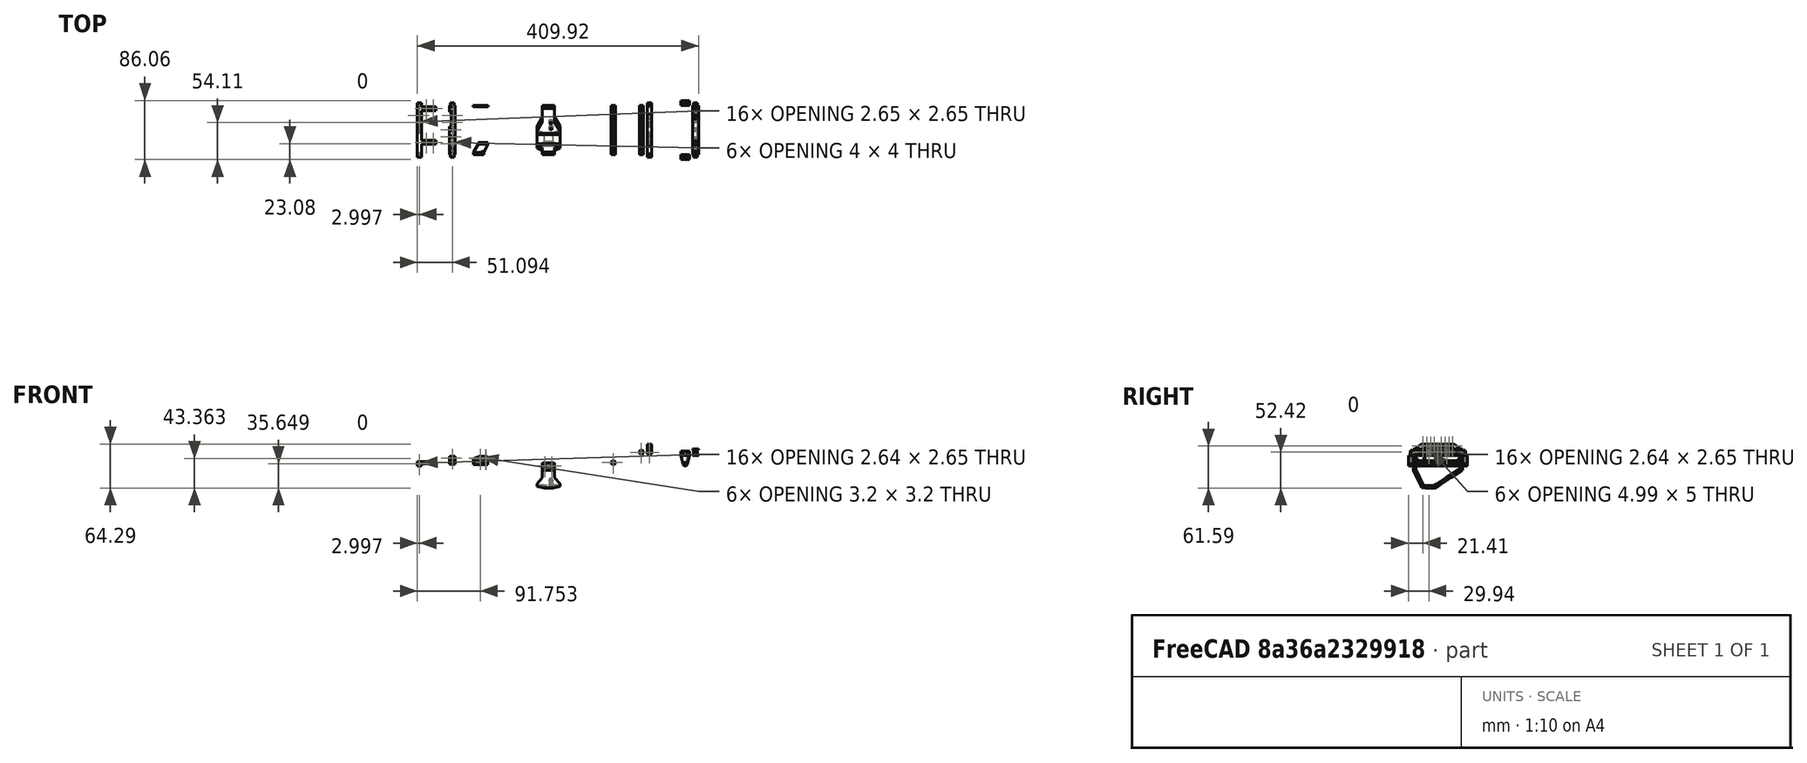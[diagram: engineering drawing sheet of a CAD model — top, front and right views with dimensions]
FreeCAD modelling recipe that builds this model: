
FCSTD DOCUMENT  (FreeCAD 1.0R39109 (Git))
Label: TF2
License: All rights reserved
LicenseURL: https://en.wikipedia.org/wiki/All_rights_reserved
objects: Part::Feature×4, Part::Refine×2, Mesh::Feature×1
note: 6 computed .brp shape members not serialized (recipe doc carries the construction recipe); baked Part::Feature solids carry a one-line shape summary decoded from their .brp

FEATURE [Mesh::Feature] Trail_Finder_2_Chassis
FEATURE [Part::Feature] Trail_Finder_2_Chassis001
  shape: bbox 445.6 x 96 x 74.94 mm, 36120 faces, 0 solids (baked)
FEATURE [Part::Feature] Trail_Finder_2_Chassis001_solid  label="Trail_Finder_2_Chassis001 (Solid)"
  shape: bbox 445.6 x 96 x 74.94 mm, 36104 faces (baked)
FEATURE [Part::Refine] Trail_Finder_2_Chassis001_solid001  label="Trail_Finder_2_Chassis001 (Solid)001"
  Source = -> Trail_Finder_2_Chassis001_solid
FEATURE [Part::Feature] Trail_Finder_2_Chassis002
  shape: bbox 445.8 x 96.21 x 75.15 mm, 36120 faces, 0 solids (baked)
FEATURE [Part::Refine] Trail_Finder_2_Chassis003
  Source = -> Trail_Finder_2_Chassis002
FEATURE [Part::Feature] Trail_Finder_2_Chassis003_solid  label="Trail_Finder_2_Chassis003 (Solid)"
  shape: bbox 445.7 x 96.1 x 75.04 mm, 11891 faces (baked)
